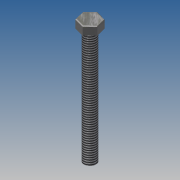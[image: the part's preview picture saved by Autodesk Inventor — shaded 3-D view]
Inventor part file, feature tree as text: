
AUTODESK INVENTOR PART (.ipt)
format: ipt  version: 2014 SP1 (Build 180222100, 222)  size: 97,280 bytes
history: native  units: in
note: dims shown in document units (in); Inventor stores cm internally (conversion verified against a paired STEP export)
features: extrude x2, sketch x2, fillet x1, thread x1
ambient origin geometry x8: Origin, YZ Plane, XZ Plane, XY Plane, X Axis, Y Axis, Z Axis, Center Point
bodies: Solid1 (feature_tree)
feature tree (6):
  extrude  "Extrusion1"  Depth=0.03in
  fillet  "Fillet1"  Radius=0.366in
  extrude  "Extrusion2"  Depth=0.55in TaperAngle=0.0deg
  thread  "Thread1"  [1 undecoded]
  sketch  "Sketch1"  dims[d0=0.25in d1=0.0in d2=0.03in d3=0.366in]
  sketch  "Sketch2"  dims[d4=3.5in d5=0.0in d6=1.0in d7=0.0in d8=0.55in]
note: 1 required parameter value undecoded (feature->parameter linkage not recoverable at this tier; creation-order binding heuristic only, values carry confidence <= 0.55)
